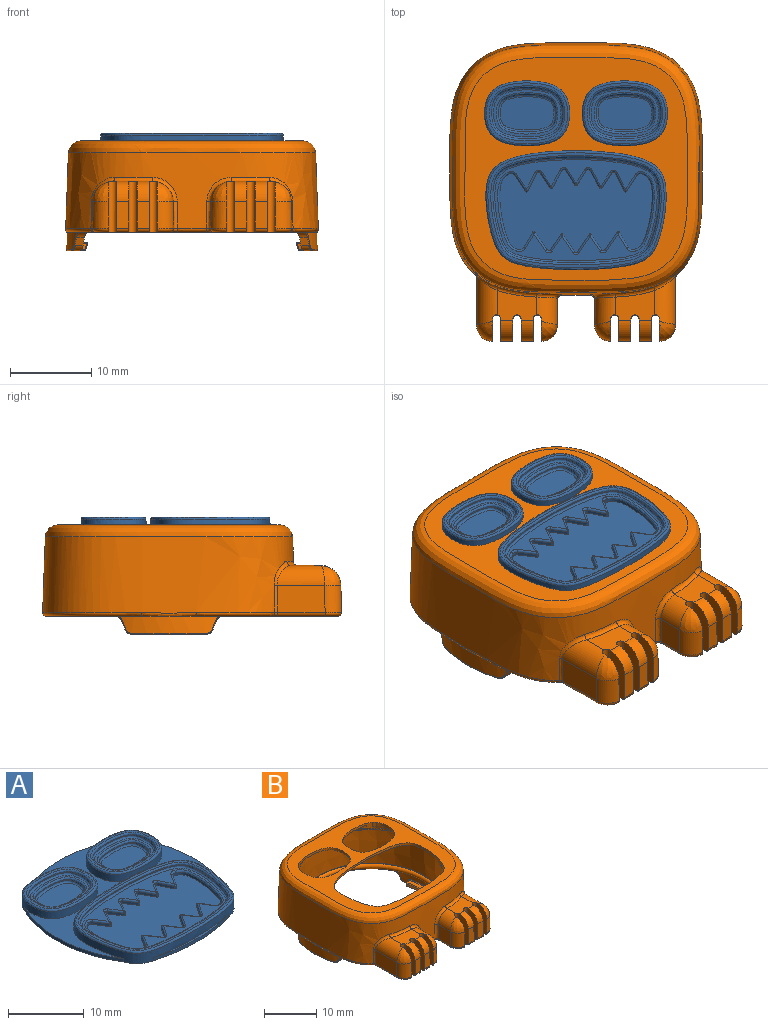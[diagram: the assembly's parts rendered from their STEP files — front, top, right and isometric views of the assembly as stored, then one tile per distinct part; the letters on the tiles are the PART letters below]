
ASSEMBLY  parts=2 mates=1
PART A: 119 faces, bbox 25.6x25.6x2.2 mm
  f0: plane 21.64x14.15mm, normal (0,0,1), area 21.1mm2, adj f114,f116
  f1: plane 9.97x7.48mm, normal (0,0,1), area 9.6mm2, adj f27,f29
  f2: plane 9.97x7.48mm, normal (0,0,1), area 9.6mm2, adj f25,f30
  f3: cylinder r=17.94mm len=17.52mm, axis (0,0,-1), area 9.2mm2, adj f6,f7,f8,f12
  f4: cylinder r=17.8mm len=18mm, axis (0,0,-1), area 9.4mm2, adj f6,f7,f11,f12
  f5: cylinder r=17.94mm len=17.52mm, axis (0,0,-1), area 9.2mm2, adj f6,f7,f8,f11
  f6: plane 25.63x22.38mm, normal (0,0,1), area 121.4mm2, adj f3,f4,f5,f8,f11,f12
  f7: plane 25.63x25.59mm, normal (0,0,-1), area 546.4mm2, adj f3,f4,f5,f8,f9,f11,f12,f117
  f8: extruded ~22.13x14.64mm, area 79.2mm2, adj f3,f5,f6,f7,f9,f10,f116
  f9: cylinder r=24.02mm len=14.06mm, axis (0,0,-1), area 7.1mm2, adj f7,f8,f10
  f10: plane 14.76x1.4mm, normal (0,0,1), area 3.3mm2, adj f8,f9
  f11: extruded ~10.45x7.96mm, area 37.8mm2, adj f4,f5,f6,f7,f29
  f12: extruded ~10.46x7.97mm, area 37.7mm2, adj f3,f4,f6,f7,f30
  f13: extruded ~8.77x6.28mm, area 3.7mm2, adj f25,f26
  f14: plane 8.27x5.78mm, normal (0,0,1), area 7.7mm2, adj f21,f26
  f15: extruded ~8.77x6.28mm, area 3.7mm2, adj f27,f28
  f16: plane 8.27x5.78mm, normal (0,0,1), area 7.7mm2, adj f22,f28
  f17: extruded ~7.06x4.57mm, area 2.9mm2, adj f22,f24
  f18: plane 6.57x4.08mm, normal (0,0,1), area 23.2mm2, adj f24
  f19: extruded ~7.06x4.57mm, area 2.9mm2, adj f21,f23
  f20: plane 6.57x4.08mm, normal (0,0,1), area 23.2mm2, adj f23
  f21: bspline ~7.57x5.08mm, area 7.9mm2, adj f14,f19
  f22: bspline ~7.57x5.08mm, area 7.9mm2, adj f16,f17
  f23: bspline ~7.07x4.59mm, area 7.4mm2, adj f19,f20
  f24: bspline ~7.07x4.59mm, area 7.4mm2, adj f17,f18
  f25: bspline ~9.27x6.78mm, area 10mm2, adj f2,f13
  f26: bspline ~8.77x6.28mm, area 9.5mm2, adj f13,f14
  f27: bspline ~9.27x6.78mm, area 10mm2, adj f1,f15
  f28: bspline ~8.77x6.28mm, area 9.5mm2, adj f15,f16
  f29: bspline ~10.47x7.98mm, area 11.6mm2, adj f1,f11
  f30: bspline ~10.47x7.98mm, area 11.6mm2, adj f2,f12
  f31: extruded ~20.4x12.91mm, area 8.6mm2, adj f114,f115
  f32: plane 19.94x12.45mm, normal (0,0,1), area 60.1mm2, adj f75,f76,f77,f78,f79,f80,f82,f83
  f33: plane 18.75x10.19mm, normal (0,0,1), area 141mm2, adj f34,f35,f36,f37,f38,f39,f40,f41
  f34: plane 1.89x1.14mm, normal (0.86,0.52,0), area 0.9mm2, adj f33,f68,f72,f84
  f35: plane 1.81x1.16mm, normal (0.84,-0.54,0), area 0.9mm2, adj f33,f36,f59,f87
  f36: cylinder r=0.25mm len=0.43mm, axis (0,0,1), area 0.2mm2, adj f33,f35,f37,f85
  f37: plane 2.17x1.2mm, normal (-0.88,-0.48,0), area 1mm2, adj f33,f36,f63,f83
  f38: plane 2.17x1.2mm, normal (0.88,-0.48,0), area 1mm2, adj f33,f39,f58,f95
  f39: cylinder r=0.25mm len=0.43mm, axis (0,0,1), area 0.2mm2, adj f33,f38,f40,f93
  f40: plane 1.81x1.16mm, normal (-0.84,-0.54,0), area 0.9mm2, adj f33,f39,f59,f91
  f41: plane 2.23x1.11mm, normal (0.89,-0.45,0), area 1mm2, adj f33,f42,f57,f103
  f42: cylinder r=0.25mm len=0.43mm, axis (0,0,1), area 0.2mm2, adj f33,f41,f43,f101
  f43: plane 1.89x1.23mm, normal (-0.84,-0.55,0), area 0.9mm2, adj f33,f42,f58,f99
  f44: plane 1.89x1.14mm, normal (-0.86,0.52,0), area 0.9mm2, adj f33,f52,f56,f112
  f45: plane 1.92x1.29mm, normal (-0.83,0.56,0), area 0.9mm2, adj f33,f46,f51,f104
  f46: cylinder r=0.25mm len=0.41mm, axis (0,0,1), area 0.2mm2, adj f33,f45,f47,f106
  f47: plane 2.21x1.5mm, normal (0.83,0.56,0), area 1.1mm2, adj f33,f46,f52,f108
  f48: plane 2.15x1.43mm, normal (-0.83,0.55,0), area 1mm2, adj f33,f49,f73,f96
  f49: cylinder r=0.21mm len=0.4mm, axis (0,0,1), area 0.2mm2, adj f33,f48,f50,f98
  f50: plane 2.15x1.43mm, normal (0.83,0.55,0), area 1mm2, adj f33,f49,f51,f100
  f51: cylinder r=0.15mm len=0.4mm, axis (0,0,1), area 0.1mm2, adj f33,f45,f50,f102
  f52: cylinder r=0.15mm len=0.4mm, axis (0,0,1), area 0.1mm2, adj f33,f44,f47,f110
  f53: extruded ~9.27x2.15mm, area 4.1mm2, adj f33,f54,f56,f111
  f54: cylinder r=0.5mm len=0.64mm, axis (0,0,1), area 0.3mm2, adj f33,f53,f55,f109
  f55: plane 1.98x1.32mm, normal (-0.83,-0.55,0), area 1mm2, adj f33,f54,f57,f107
  f56: cylinder r=0.69mm len=0.78mm, axis (0,0,1), area 0.4mm2, adj f33,f44,f53,f113
  f57: cylinder r=0.15mm len=0.4mm, axis (0,0,1), area 0.1mm2, adj f33,f41,f55,f105
  f58: cylinder r=0.15mm len=0.4mm, axis (0,0,1), area 0.1mm2, adj f33,f38,f43,f97
  f59: cylinder r=0.15mm len=0.4mm, axis (0,0,1), area 0.1mm2, adj f33,f35,f40,f89
  f60: plane 1.89x1.23mm, normal (0.84,-0.55,0), area 0.9mm2, adj f33,f61,f63,f79
  f61: cylinder r=0.25mm len=0.43mm, axis (0,0,1), area 0.2mm2, adj f33,f60,f62,f77
  f62: plane 2.23x1.11mm, normal (-0.89,-0.45,0), area 1mm2, adj f33,f61,f67,f75
  f63: cylinder r=0.15mm len=0.4mm, axis (0,0,1), area 0.1mm2, adj f33,f37,f60,f81
  f64: plane 1.97x1.31mm, normal (0.83,-0.55,0), area 0.9mm2, adj f33,f65,f67,f76
  f65: cylinder r=0.52mm len=0.67mm, axis (0,0,1), area 0.3mm2, adj f33,f64,f66,f78
  f66: extruded ~9.26x2.15mm, area 4.1mm2, adj f33,f65,f68,f80
  f67: cylinder r=0.15mm len=0.4mm, axis (0,0,1), area 0.1mm2, adj f33,f62,f64,f74
  f68: cylinder r=0.69mm len=0.78mm, axis (0,0,1), area 0.4mm2, adj f33,f34,f66,f82
  f69: plane 2.21x1.5mm, normal (-0.83,0.56,0), area 1.1mm2, adj f33,f70,f72,f88
  f70: cylinder r=0.25mm len=0.41mm, axis (0,0,1), area 0.2mm2, adj f33,f69,f71,f90
  f71: plane 1.92x1.29mm, normal (0.83,0.56,0), area 0.9mm2, adj f33,f70,f73,f92
  f72: cylinder r=0.15mm len=0.4mm, axis (0,0,1), area 0.1mm2, adj f33,f34,f69,f86
  f73: cylinder r=0.15mm len=0.4mm, axis (0,0,1), area 0.1mm2, adj f33,f48,f71,f94
  f74: bspline ~0.5x0.27mm, area 0.1mm2, adj f67,f75,f76
  f75: cylinder r=0.25mm len=2.34mm, axis (0.45,-0.89,0), area 0.9mm2, adj f32,f62,f74,f77
  f76: cylinder r=0.25mm len=2.11mm, axis (0.55,0.83,0), area 0.9mm2, adj f32,f64,f74,f78
  f77: torus R=0.5mm, axis (0,0,1), area 0.3mm2, adj f32,f61,f75,f79
  f78: torus R=0.77mm, axis (0,0,1), area 0.3mm2, adj f32,f65,f76,f80
  f79: cylinder r=0.25mm len=2.02mm, axis (0.55,0.84,0), area 0.9mm2, adj f32,f60,f77,f81
  f80: bspline ~10.14x2.62mm, area 4.1mm2, adj f32,f66,f78,f82
  f81: bspline ~0.49x0.27mm, area 0.1mm2, adj f63,f79,f83
  f82: torus R=0.94mm, axis (0,0,1), area 0.4mm2, adj f32,f68,f80,f84
  f83: cylinder r=0.25mm len=2.29mm, axis (0.48,-0.88,0), area 0.9mm2, adj f32,f37,f81,f85
  f84: cylinder r=0.25mm len=2.02mm, axis (-0.52,0.86,0), area 0.8mm2, adj f32,f34,f82,f86
  f85: torus R=0.5mm, axis (0,0,1), area 0.3mm2, adj f32,f36,f83,f87
  f86: bspline ~0.46x0.27mm, area 0.1mm2, adj f72,f84,f88
  f87: cylinder r=0.25mm len=1.94mm, axis (0.54,0.84,0), area 0.8mm2, adj f32,f35,f85,f89
  f88: cylinder r=0.25mm len=2.35mm, axis (-0.56,-0.83,0), area 1mm2, adj f32,f69,f86,f90
  f89: bspline ~0.46x0.27mm, area 0.1mm2, adj f59,f87,f91
  f90: torus R=0.5mm, axis (0,0,1), area 0.3mm2, adj f32,f70,f88,f92
  f91: cylinder r=0.25mm len=1.94mm, axis (0.54,-0.84,0), area 0.8mm2, adj f32,f40,f89,f93
  f92: cylinder r=0.25mm len=2.06mm, axis (-0.56,0.83,0), area 0.9mm2, adj f32,f71,f90,f94
  f93: torus R=0.5mm, axis (0,0,1), area 0.3mm2, adj f32,f39,f91,f95
  f94: bspline ~0.45x0.27mm, area 0.1mm2, adj f73,f92,f96
  f95: cylinder r=0.25mm len=2.29mm, axis (0.48,0.88,0), area 0.9mm2, adj f32,f38,f93,f97
  f96: cylinder r=0.25mm len=2.29mm, axis (-0.55,-0.83,0), area 1mm2, adj f32,f48,f94,f98
  f97: bspline ~0.49x0.27mm, area 0.1mm2, adj f58,f95,f99
  f98: torus R=0.46mm, axis (0,0,1), area 0.2mm2, adj f32,f49,f96,f100
  f99: cylinder r=0.25mm len=2.02mm, axis (0.55,-0.84,0), area 0.9mm2, adj f32,f43,f97,f101
  f100: cylinder r=0.25mm len=2.29mm, axis (-0.55,0.83,0), area 1mm2, adj f32,f50,f98,f102
  f101: torus R=0.5mm, axis (0,0,1), area 0.3mm2, adj f32,f42,f99,f103
  f102: bspline ~0.45x0.27mm, area 0.1mm2, adj f51,f100,f104
  f103: cylinder r=0.25mm len=2.34mm, axis (0.45,0.89,0), area 0.9mm2, adj f32,f41,f101,f105
  f104: cylinder r=0.25mm len=2.06mm, axis (-0.56,-0.83,0), area 0.9mm2, adj f32,f45,f102,f106
  f105: bspline ~0.5x0.27mm, area 0.1mm2, adj f57,f103,f107
  f106: torus R=0.5mm, axis (0,0,1), area 0.3mm2, adj f32,f46,f104,f108
  f107: cylinder r=0.25mm len=2.12mm, axis (0.55,-0.83,0), area 0.9mm2, adj f32,f55,f105,f109
  f108: cylinder r=0.25mm len=2.35mm, axis (-0.56,0.83,0), area 1mm2, adj f32,f47,f106,f110
  f109: torus R=0.75mm, axis (0,0,1), area 0.3mm2, adj f32,f54,f107,f111
  f110: bspline ~0.46x0.27mm, area 0.1mm2, adj f52,f108,f112
  f111: bspline ~10.15x2.61mm, area 4.2mm2, adj f32,f53,f109,f113
  f112: cylinder r=0.25mm len=2.02mm, axis (-0.52,-0.86,0), area 0.8mm2, adj f32,f44,f110,f113
  f113: torus R=0.94mm, axis (0,0,1), area 0.4mm2, adj f32,f56,f111,f112
  f114: bspline ~20.94x13.45mm, area 22.7mm2, adj f0,f31
  f115: bspline ~20.44x12.95mm, area 22.3mm2, adj f31,f32
  f116: bspline ~22.14x14.65mm, area 24.4mm2, adj f0,f8
  f117: cone r=1.05mm half-angle=2deg, axis (0,0,1), area 1.3mm2, adj f7,f118
  f118: plane 2.09x2.09mm, normal (0,0,-1), area 3.4mm2, adj f117
PART B: 282 faces, bbox 35.3x38.8x19.9 mm
  f0: plane 30.07x17.37mm, normal (0,0,-1), area 95.5mm2, adj f13,f14,f15,f16,f17,f20,f21,f27
  f1: plane 4.87x3.68mm, normal (0,0,1), area 14.3mm2, adj f10,f11,f150,f151,f154,f218,f220,f221
  f2: plane 3.29x1.5mm, normal (0,-1,0.02), area 4.9mm2, adj f10,f15,f220,f225
  f3: plane 3.29x1.5mm, normal (0,-1,0.02), area 4.9mm2, adj f11,f16,f222,f226
  f4: plane 4.87x3.68mm, normal (0,0,1), area 14.3mm2, adj f8,f145,f147,f149,f159,f228,f229,f231
  f5: plane 3.29x1.5mm, normal (0,-1,0.02), area 4.9mm2, adj f8,f13,f232,f233
  f6: cylinder r=2mm len=3.3mm, axis (-0.02,-0.02,-1), area 10.2mm2, adj f12,f17,f139,f219
  f7: cylinder r=2mm len=3.3mm, axis (0.02,-0.02,-1), area 10.2mm2, adj f9,f14,f138,f223
  f8: cylinder r=2.5mm len=2.5mm, axis (1,0,0), area 5.8mm2, adj f4,f5,f232,f233
  f9: bspline ~2.64x2.42mm, area 4.8mm2, adj f7,f150,f223
  f10: cylinder r=2.5mm len=2.5mm, axis (-1,0,0), area 5.8mm2, adj f1,f2,f220,f225
  f11: cylinder r=2.5mm len=2.5mm, axis (-1,0,0), area 5.8mm2, adj f1,f3,f222,f226
  f12: bspline ~2.64x2.42mm, area 4.8mm2, adj f6,f151,f219
  f13: cylinder r=0.5mm len=1.5mm, axis (1,0,0), area 1.2mm2, adj f0,f5,f232,f233
  f14: bspline ~2x1.99mm, area 2.3mm2, adj f0,f7,f173,f223
  f15: cylinder r=0.5mm len=1.5mm, axis (-1,0,0), area 1.2mm2, adj f0,f2,f220,f225
  f16: cylinder r=0.5mm len=1.5mm, axis (-1,0,0), area 1.2mm2, adj f0,f3,f222,f226
  f17: bspline ~2x1.99mm, area 2.3mm2, adj f0,f6,f178,f219
  f18: plane 30.07x11.72mm, normal (0,0,-1), area 45mm2, adj f20,f21,f27,f34,f39,f174,f186,f187
  f19: bspline ~31.02x31.02mm, area 862mm2, adj f152,f153,f154,f155,f156,f157,f158,f159
  f20: cone r=15.12mm half-angle=2deg, axis (0,0,-1), area 23.5mm2, adj f0,f18,f175,f180,f181,f182,f183,f184
  f21: cone r=15.12mm half-angle=2deg, axis (0,0,-1), area 23.5mm2, adj f0,f18,f172,f187,f188,f189,f190,f191
  f22: plane 13.19x2.44mm, normal (0,0,-1), area 4.6mm2, adj f102,f108
  f23: plane 13.37x1.8mm, normal (0,0,-1), area 4.6mm2, adj f103,f109
  f24: plane 13.19x2.44mm, normal (0,0,-1), area 4.6mm2, adj f104,f106
  f25: plane 10.51x1.08mm, normal (0,0,-1), area 3.6mm2, adj f101,f107
  f26: plane 27.38x27.38mm, normal (0,0,1), area 266.9mm2, adj f92,f93,f94,f95,f96,f97,f98,f99
  f27: cone r=14.12mm half-angle=2deg, axis (0,0,-1), area 59.9mm2, adj f0,f18,f28,f29,f30,f31,f32,f33
  f28: plane 1.15x0.94mm, normal (0,-0.94,-0.34), area 1mm2, adj f27,f38,f40,f181
  f29: plane 1.15x0.94mm, normal (0,0.94,-0.34), area 1mm2, adj f27,f39,f41,f185
  f30: plane 9.02x2.13mm, normal (0,0,-1), area 13.4mm2, adj f27,f40,f41,f55,f58,f61,f81,f87
  f31: plane 1.15x0.94mm, normal (0,-0.94,-0.34), area 1mm2, adj f27,f35,f37,f192
  f32: plane 1.15x0.94mm, normal (0,0.94,-0.34), area 1mm2, adj f27,f34,f36,f188
  f33: plane 9.02x2.13mm, normal (0,0,-1), area 13.4mm2, adj f27,f36,f37,f62,f63,f64,f74,f80
  f34: cylinder r=1mm len=1.45mm, axis (1,0,0), area 1.2mm2, adj f18,f27,f32,f187
  f35: cylinder r=1mm len=1.45mm, axis (1,0,0), area 1.2mm2, adj f0,f27,f31,f193
  f36: cylinder r=1mm len=1.25mm, axis (1,0,0), area 1.1mm2, adj f27,f32,f33,f189
  f37: cylinder r=1mm len=1.25mm, axis (1,0,0), area 1.1mm2, adj f27,f31,f33,f191
  f38: cylinder r=1mm len=1.45mm, axis (-1,0,0), area 1.2mm2, adj f0,f27,f28,f180
  f39: cylinder r=1mm len=1.45mm, axis (-1,0,0), area 1.2mm2, adj f18,f27,f29,f186
  f40: cylinder r=1mm len=1.25mm, axis (-1,0,0), area 1.1mm2, adj f27,f28,f30,f182
  f41: cylinder r=1mm len=1.25mm, axis (-1,0,0), area 1.1mm2, adj f27,f29,f30,f184
  f42: plane 7.09x1.32mm, normal (0,0,1), area 6.2mm2, adj f50,f51,f52,f84
  f43: cone r=13.14mm half-angle=20.9deg, axis (0,0,-1), area 5.4mm2, adj f51,f56,f57,f61
  f44: plane 0.91x0.75mm, normal (0.26,-0.97,0), area 0.6mm2, adj f50,f55,f56,f86
  f45: plane 0.91x0.75mm, normal (0.26,0.97,0), area 0.6mm2, adj f52,f57,f58,f82
  f46: plane 7.09x1.32mm, normal (0,0,1), area 6.2mm2, adj f68,f69,f73,f77
  f47: cone r=13.14mm half-angle=20.9deg, axis (0,0,-1), area 5.4mm2, adj f64,f67,f70,f73
  f48: plane 0.91x0.75mm, normal (-0.26,0.97,0), area 0.6mm2, adj f62,f67,f68,f75
  f49: plane 0.91x0.75mm, normal (-0.26,-0.97,0), area 0.6mm2, adj f63,f69,f70,f79
  f50: cylinder r=0.15mm len=0.92mm, axis (0.97,0.26,0), area 0.2mm2, adj f42,f44,f53,f85
  f51: torus R=13.36mm, axis (0,0,1), area 1.9mm2, adj f42,f43,f53,f54
  f52: cylinder r=0.15mm len=0.92mm, axis (-0.97,0.26,0), area 0.2mm2, adj f42,f45,f54,f83
  f53: sphere r=0.15mm, area 0mm2, adj f50,f51,f56
  f54: sphere r=0.15mm, area 0mm2, adj f51,f52,f57
  f55: cylinder r=0.15mm len=0.68mm, axis (-0.97,-0.26,0), area 0.2mm2, adj f30,f44,f59,f87
  f56: bspline ~10.31x3.91mm, area 0.2mm2, adj f43,f44,f53,f59
  f57: bspline ~10.31x3.91mm, area 0.2mm2, adj f43,f45,f54,f60
  f58: cylinder r=0.15mm len=0.68mm, axis (0.97,-0.26,0), area 0.2mm2, adj f30,f45,f60,f81
  f59: sphere r=0.15mm, area 0mm2, adj f55,f56,f61
  f60: sphere r=0.15mm, area 0mm2, adj f57,f58,f61
  f61: torus R=13.65mm, axis (0,0,-1), area 1.2mm2, adj f30,f43,f59,f60
  f62: cylinder r=0.15mm len=0.68mm, axis (-0.97,-0.26,0), area 0.2mm2, adj f33,f48,f65,f74
  f63: cylinder r=0.15mm len=0.68mm, axis (0.97,-0.26,0), area 0.2mm2, adj f33,f49,f66,f80
  f64: torus R=13.65mm, axis (0,0,-1), area 1.2mm2, adj f33,f47,f65,f66
  f65: sphere r=0.15mm, area 0mm2, adj f62,f64,f67
  f66: sphere r=0.15mm, area 0mm2, adj f63,f64,f70
  f67: bspline ~10.31x3.91mm, area 0.2mm2, adj f47,f48,f65,f71
  f68: cylinder r=0.15mm len=0.92mm, axis (0.97,0.26,0), area 0.2mm2, adj f46,f48,f71,f76
  f69: cylinder r=0.15mm len=0.92mm, axis (-0.97,0.26,0), area 0.2mm2, adj f46,f49,f72,f78
  f70: bspline ~10.31x3.91mm, area 0.2mm2, adj f47,f49,f66,f72
  f71: sphere r=0.15mm, area 0.1mm2, adj f67,f68,f73
  f72: sphere r=0.15mm, area 0mm2, adj f69,f70,f73
  f73: torus R=13.36mm, axis (0,0,1), area 1.9mm2, adj f46,f47,f71,f72
  f74: bspline ~0.35x0.34mm, area 0mm2, adj f27,f33,f62,f75
  f75: bspline ~3.76x0.27mm, area 0.2mm2, adj f27,f48,f74,f76
  f76: bspline ~0.37x0.32mm, area 0.1mm2, adj f27,f68,f75,f77
  f77: torus R=14.26mm, axis (0,0,1), area 1.7mm2, adj f27,f46,f76,f78
  f78: bspline ~0.37x0.34mm, area 0.1mm2, adj f27,f69,f77,f79
  f79: bspline ~3.76x0.27mm, area 0.2mm2, adj f27,f49,f78,f80
  f80: bspline ~0.35x0.34mm, area 0mm2, adj f27,f33,f63,f79
  f81: bspline ~0.35x0.34mm, area 0mm2, adj f27,f30,f58,f82
  f82: bspline ~3.76x0.27mm, area 0.2mm2, adj f27,f45,f81,f83
  f83: bspline ~0.37x0.34mm, area 0.1mm2, adj f27,f52,f82,f84
  f84: torus R=14.26mm, axis (0,0,1), area 1.7mm2, adj f27,f42,f83,f85
  f85: bspline ~0.37x0.32mm, area 0.1mm2, adj f27,f50,f84,f86
  f86: bspline ~3.76x0.27mm, area 0.2mm2, adj f27,f44,f85,f87
  f87: bspline ~0.35x0.34mm, area 0mm2, adj f27,f30,f55,f86
  f88: plane 28.65x28.65mm, normal (0,0,1), area 10.1mm2, adj f90,f91
  f89: plane 28.73x28.73mm, normal (0,0,-1), area 13.5mm2, adj f27,f90
  f90: torus R=14.21mm, axis (0,0,-1), area 150.5mm2, adj f88,f89
  f91: cone r=14.12mm half-angle=2deg, axis (0,0,-1), area 723mm2, adj f88,f92,f93,f94,f95,f96,f97,f98
  f92: extruded ~10.44x7.96mm, area 16.7mm2, adj f26,f91,f93,f102,f103,f105,f108,f109
  f93: cylinder r=14.02mm len=1mm, axis (0,0,-1), area 0.8mm2, adj f26,f91,f92
  f94: extruded ~10.44x7.96mm, area 16.7mm2, adj f26,f91,f95,f103,f104,f105,f106,f109
  f95: cylinder r=14.02mm len=1mm, axis (0,0,-1), area 0.8mm2, adj f26,f91,f94
  f96: extruded ~22.12x13.12mm, area 24.8mm2, adj f26,f91,f97,f99,f102,f104,f105,f106
  f97: cylinder r=14.02mm len=1mm, axis (0,0,-1), area 0.9mm2, adj f26,f91,f96,f98
  f98: extruded ~17.62x1.72mm, area 11.4mm2, adj f26,f91,f97,f99,f100,f101,f107
  f99: cylinder r=14.02mm len=1mm, axis (0,0,-1), area 0.9mm2, adj f26,f91,f96,f98
  f100: plane 14.76x1.4mm, normal (0,0,-1), area 3.3mm2, adj f98,f101
  f101: cylinder r=24.02mm len=14.06mm, axis (0,0,-1), area 7.3mm2, adj f25,f98,f100,f107
  f102: cylinder r=17.94mm len=17.52mm, axis (0,0,-1), area 9.5mm2, adj f22,f92,f96,f105,f108
  f103: cylinder r=17.8mm len=18mm, axis (0,0,-1), area 9.8mm2, adj f23,f92,f94,f105,f109
  f104: cylinder r=17.94mm len=17.52mm, axis (0,0,-1), area 9.5mm2, adj f24,f94,f96,f105,f106
  f105: plane 25.63x22.38mm, normal (0,0,-1), area 121.4mm2, adj f92,f94,f96,f102,f103,f104
  f106: torus R=13.29mm, axis (0,0,1), area 22.2mm2, adj f24,f91,f94,f96,f104
  f107: torus R=13.29mm, axis (0,0,1), area 17.8mm2, adj f25,f91,f98,f101
  f108: torus R=13.29mm, axis (0,0,1), area 22.2mm2, adj f22,f91,f92,f96,f102
  f109: torus R=13.29mm, axis (0,0,1), area 22.6mm2, adj f23,f91,f92,f94,f103
  f110: plane 6.72x6.72mm, normal (0,0,-1), area 12mm2, adj f111,f112,f113,f114,f115,f116
  f111: plane 9.26x1.2mm, normal (0.05,1,-0.03), area 9mm2, adj f110,f112,f116,f216
  f112: bspline ~9.26x0.79mm, area 7.5mm2, adj f110,f111,f113,f214
  f113: bspline ~9.25x6.18mm, area 79mm2, adj f110,f112,f114,f212
  f114: bspline ~9.26x0.79mm, area 7.5mm2, adj f110,f113,f115,f213
  f115: plane 9.26x1.2mm, normal (1,0.05,-0.03), area 9mm2, adj f110,f114,f116,f215
  f116: bspline ~9.41x5.67mm, area 73.3mm2, adj f110,f111,f115,f215,f216,f217
  f117: plane 6.76x6.73mm, normal (0,0,-1), area 12.1mm2, adj f118,f119,f120,f121,f122,f123
  f118: bspline ~9.26x0.81mm, area 8.3mm2, adj f117,f119,f123,f208,f210,f211
  f119: plane 9.26x1.2mm, normal (-1,-0.05,-0.03), area 9mm2, adj f117,f118,f120,f208
  f120: bspline ~9.41x5.67mm, area 73.4mm2, adj f117,f119,f121,f206,f207,f208
  f121: plane 9.26x1.2mm, normal (-0.05,-1,-0.03), area 9mm2, adj f117,f120,f122,f207
  f122: bspline ~9.26x0.79mm, area 7.5mm2, adj f117,f121,f123,f209
  f123: bspline ~9.25x6.17mm, area 78.7mm2, adj f117,f118,f122,f211
  f124: plane 6.72x6.72mm, normal (0,0,-1), area 12mm2, adj f125,f126,f127,f128,f129,f130
  f125: bspline ~9.41x6.19mm, area 79mm2, adj f124,f126,f130,f204
  f126: bspline ~9.26x0.79mm, area 7.5mm2, adj f124,f125,f127,f202
  f127: plane 9.26x1.2mm, normal (0.05,-1,-0.03), area 9mm2, adj f124,f126,f128,f200
  f128: bspline ~9.41x5.67mm, area 73.4mm2, adj f124,f127,f129,f200,f201,f203
  f129: plane 9.26x1.21mm, normal (1,-0.05,-0.03), area 9.1mm2, adj f124,f128,f130,f203
  f130: bspline ~9.26x0.79mm, area 7.5mm2, adj f124,f125,f129,f205
  f131: plane 6.76x6.73mm, normal (0,0,-1), area 12.1mm2, adj f132,f133,f134,f135,f136,f137
  f132: bspline ~9.41x6.17mm, area 78.7mm2, adj f131,f133,f137,f198
  f133: bspline ~9.26x0.79mm, area 7.5mm2, adj f131,f132,f134,f196
  f134: plane 9.26x1.21mm, normal (-0.05,1,-0.03), area 9.1mm2, adj f131,f133,f135,f194
  f135: bspline ~9.41x5.67mm, area 73.4mm2, adj f131,f134,f136,f194,f195,f197
  f136: plane 9.26x1.2mm, normal (-1,0.05,-0.03), area 9mm2, adj f131,f135,f137,f197
  f137: bspline ~9.26x0.81mm, area 8.3mm2, adj f131,f132,f136,f197,f198,f199
  f138: plane 3.29x3.27mm, normal (1,0,0.02), area 10.5mm2, adj f7,f150,f156,f173
  f139: plane 5.9x3.29mm, normal (-1,0,0.02), area 19.1mm2, adj f6,f151,f152,f178
  f140: plane 5.9x3.29mm, normal (1,0,0.02), area 19.1mm2, adj f143,f149,f161,f166
  f141: plane 3.29x3.27mm, normal (-1,0,0.02), area 10.5mm2, adj f144,f145,f157,f165
  f142: plane 3.29x1.5mm, normal (0,-1,0.02), area 4.9mm2, adj f147,f162,f228,f235
  f143: cylinder r=2mm len=3.3mm, axis (0.02,-0.02,-1), area 10.2mm2, adj f140,f148,f164,f227
  f144: cylinder r=2mm len=3.3mm, axis (-0.02,-0.02,-1), area 10.2mm2, adj f141,f146,f163,f230
  f145: cylinder r=2.5mm len=3.37mm, axis (0,-1,0), area 11.5mm2, adj f4,f141,f146,f158,f230,f231
  f146: bspline ~2.64x2.42mm, area 4.8mm2, adj f144,f145,f230
  f147: cylinder r=2.5mm len=2.5mm, axis (1,0,0), area 5.8mm2, adj f4,f142,f228,f235
  f148: bspline ~2.64x2.42mm, area 4.8mm2, adj f143,f149,f227
  f149: cylinder r=2.5mm len=5.84mm, axis (0,-1,0), area 18.8mm2, adj f4,f140,f148,f160,f227,f229
  f150: cylinder r=2.5mm len=3.37mm, axis (0,-1,0), area 11.5mm2, adj f1,f9,f138,f155,f221,f223
  f151: cylinder r=2.5mm len=5.84mm, axis (0,-1,0), area 18.8mm2, adj f1,f12,f139,f153,f218,f219
  f152: bspline ~6.79x0.58mm, area 1.4mm2, adj f19,f139,f153,f177
  f153: bspline ~3.52x2.99mm, area 2.6mm2, adj f19,f151,f152,f154
  f154: bspline ~9.61x2.13mm, area 3.7mm2, adj f1,f19,f153,f155
  f155: bspline ~3.64x3.62mm, area 3.2mm2, adj f19,f150,f154,f156
  f156: bspline ~6.89x0.74mm, area 2.6mm2, adj f19,f138,f155,f171
  f157: bspline ~6.89x0.74mm, area 2.6mm2, adj f19,f141,f158,f167
  f158: bspline ~3.64x3.62mm, area 3.2mm2, adj f19,f145,f157,f159
  f159: bspline ~9.61x2.13mm, area 3.7mm2, adj f4,f19,f158,f160
  f160: bspline ~3.52x3.47mm, area 2.6mm2, adj f19,f149,f159,f161
  f161: bspline ~6.79x0.58mm, area 1.4mm2, adj f19,f140,f160,f168
  f162: cylinder r=0.5mm len=1.5mm, axis (1,0,0), area 1.2mm2, adj f0,f142,f228,f235
  f163: bspline ~2x1.99mm, area 2.3mm2, adj f0,f144,f165,f230
  f164: bspline ~2x1.99mm, area 2.3mm2, adj f0,f143,f166,f227
  f165: cylinder r=0.5mm len=3.16mm, axis (0,-1,0), area 2.5mm2, adj f0,f141,f163,f167
  f166: cylinder r=0.5mm len=5.8mm, axis (0,-1,0), area 4.6mm2, adj f0,f140,f164,f168
  f167: bspline ~1.22x1.22mm, area 0.9mm2, adj f0,f157,f165,f169
  f168: bspline ~0.93x0.77mm, area 0.5mm2, adj f0,f161,f166,f170
  f169: bspline ~7.78x0.54mm, area 2.8mm2, adj f0,f19,f167,f171
  f170: bspline ~10.77x4mm, area 8.3mm2, adj f0,f19,f168,f172
  f171: bspline ~1.22x1.22mm, area 0.9mm2, adj f0,f156,f169,f173
  f172: bspline ~7.19x0.59mm, area 3.7mm2, adj f19,f21,f170,f174
  f173: cylinder r=0.5mm len=3.16mm, axis (0,-1,0), area 2.5mm2, adj f0,f14,f138,f171
  f174: bspline ~31.01x12.16mm, area 37.2mm2, adj f18,f19,f172,f175
  f175: bspline ~7.19x0.59mm, area 3.7mm2, adj f19,f20,f174,f176
  f176: bspline ~12x4.98mm, area 8.3mm2, adj f0,f19,f175,f177
  f177: bspline ~1.01x0.7mm, area 0.5mm2, adj f0,f152,f176,f178
  f178: cylinder r=0.5mm len=5.8mm, axis (0,-1,0), area 4.6mm2, adj f0,f17,f139,f177
  f179: bspline ~30.38x30.38mm, area 234mm2, adj f19,f26
  f180: bspline ~1.36x1.02mm, area 0.2mm2, adj f0,f20,f38,f181
  f181: bspline ~8.61x3.22mm, area 0.2mm2, adj f20,f28,f180,f182
  f182: bspline ~1.05x0.89mm, area 0.3mm2, adj f20,f40,f181,f183
  f183: torus R=15.3mm, axis (0,0,-1), area 2.2mm2, adj f20,f30,f182,f184
  f184: bspline ~1.19x0.76mm, area 0.3mm2, adj f20,f41,f183,f185
  f185: bspline ~8.61x3.22mm, area 0.2mm2, adj f20,f29,f184,f186
  f186: bspline ~1.36x1.02mm, area 0.2mm2, adj f18,f20,f39,f185
  f187: bspline ~1.36x1.02mm, area 0.2mm2, adj f18,f21,f34,f188
  f188: bspline ~8.61x3.22mm, area 0.2mm2, adj f21,f32,f187,f189
  f189: bspline ~1.05x0.89mm, area 0.3mm2, adj f21,f36,f188,f190
  f190: torus R=15.3mm, axis (0,0,-1), area 2.2mm2, adj f21,f33,f189,f191
  f191: bspline ~1.19x0.76mm, area 0.3mm2, adj f21,f37,f190,f192
  f192: bspline ~8.61x3.22mm, area 0.2mm2, adj f21,f31,f191,f193
  f193: bspline ~1.36x1.02mm, area 0.2mm2, adj f0,f21,f35,f192
  f194: cylinder r=0.15mm len=1mm, axis (1,0.05,0), area 0.2mm2, adj f0,f134,f135,f195,f196
  f195: bspline ~6.06x5.87mm, area 1.8mm2, adj f0,f135,f194,f197
  f196: bspline ~0.92x0.51mm, area 0.2mm2, adj f0,f133,f194,f198
  f197: cylinder r=0.15mm len=1mm, axis (0.05,1,0), area 0.2mm2, adj f0,f135,f136,f137,f195,f199
  f198: bspline ~7.34x6.83mm, area 2mm2, adj f0,f132,f137,f196,f199
  f199: bspline ~0.89x0.64mm, area 0.2mm2, adj f0,f137,f197,f198
  f200: cylinder r=0.15mm len=1mm, axis (-1,-0.05,0), area 0.2mm2, adj f18,f127,f128,f201,f202
  f201: bspline ~6.06x5.87mm, area 1.8mm2, adj f18,f128,f200,f203
  f202: bspline ~0.92x0.51mm, area 0.2mm2, adj f18,f126,f200,f204
  f203: cylinder r=0.15mm len=1mm, axis (-0.05,-1,0), area 0.2mm2, adj f18,f128,f129,f201,f205
  f204: bspline ~8.01x8.01mm, area 2mm2, adj f18,f125,f202,f205
  f205: bspline ~0.86x0.62mm, area 0.2mm2, adj f18,f130,f203,f204
  f206: bspline ~6.06x5.87mm, area 1.8mm2, adj f18,f120,f207,f208
  f207: cylinder r=0.15mm len=1mm, axis (-1,0.05,0), area 0.2mm2, adj f18,f120,f121,f206,f209
  f208: cylinder r=0.15mm len=1mm, axis (-0.05,1,0), area 0.2mm2, adj f18,f118,f119,f120,f206,f210
  f209: bspline ~0.86x0.62mm, area 0.2mm2, adj f18,f122,f207,f211
  f210: bspline ~0.91x0.56mm, area 0.2mm2, adj f18,f118,f208,f211
  f211: bspline ~7.34x6.83mm, area 2mm2, adj f18,f118,f123,f209,f210
  f212: bspline ~7.48x7.06mm, area 2mm2, adj f0,f113,f213,f214
  f213: bspline ~0.92x0.51mm, area 0.2mm2, adj f0,f114,f212,f215
  f214: bspline ~0.86x0.62mm, area 0.2mm2, adj f0,f112,f212,f216
  f215: cylinder r=0.15mm len=1mm, axis (0.05,-1,0), area 0.2mm2, adj f0,f115,f116,f213,f217
  f216: cylinder r=0.15mm len=1mm, axis (1,-0.05,0), area 0.2mm2, adj f0,f111,f116,f214,f217
  f217: bspline ~6.06x5.87mm, area 1.8mm2, adj f0,f116,f215,f216
  f218: cylinder r=0.5mm len=6.25mm, axis (0,0,-1), area 9.8mm2, adj f0,f1,f151,f219,f220
  f219: plane 8.03x4.59mm, normal (1,0,0), area 15.4mm2, adj f0,f6,f12,f17,f151,f218
  f220: plane 6.25x2.74mm, normal (-1,0,0), area 15.5mm2, adj f0,f1,f2,f10,f15,f218
  f221: cylinder r=0.5mm len=6.25mm, axis (0,0,-1), area 9.8mm2, adj f0,f1,f150,f222,f223
  f222: plane 6.25x2.74mm, normal (1,0,0), area 15.5mm2, adj f0,f1,f3,f11,f16,f221
  f223: plane 8.03x4.59mm, normal (-1,0,0), area 15.4mm2, adj f0,f7,f9,f14,f150,f221
  f224: cylinder r=0.5mm len=6.25mm, axis (0,0,-1), area 9.8mm2, adj f0,f1,f225,f226
  f225: plane 6.25x2.74mm, normal (1,0,0), area 15.5mm2, adj f0,f1,f2,f10,f15,f224
  f226: plane 6.25x2.74mm, normal (-1,0,0), area 15.5mm2, adj f0,f1,f3,f11,f16,f224
  f227: plane 8.03x4.59mm, normal (-1,0,0), area 15.4mm2, adj f0,f143,f148,f149,f164,f229
  f228: plane 6.25x2.74mm, normal (1,0,0), area 15.5mm2, adj f0,f4,f142,f147,f162,f229
  f229: cylinder r=0.5mm len=6.25mm, axis (0,0,-1), area 9.8mm2, adj f0,f4,f149,f227,f228
  f230: plane 8.03x4.59mm, normal (1,0,0), area 15.4mm2, adj f0,f144,f145,f146,f163,f231
  f231: cylinder r=0.5mm len=6.25mm, axis (0,0,-1), area 9.8mm2, adj f0,f4,f145,f230,f232
  f232: plane 6.25x2.74mm, normal (-1,0,0), area 15.5mm2, adj f0,f4,f5,f8,f13,f231
  f233: plane 6.25x2.74mm, normal (1,0,0), area 15.5mm2, adj f0,f4,f5,f8,f13,f234
  f234: cylinder r=0.5mm len=6.25mm, axis (0,0,-1), area 9.8mm2, adj f0,f4,f233,f235
  f235: plane 6.25x2.74mm, normal (-1,0,0), area 15.5mm2, adj f0,f4,f142,f147,f162,f234
  f236: cylinder r=0.15mm len=5mm, axis (0,0,-1), area 1.9mm2, adj f237,f246,f247,f274
  f237: plane 5x2.1mm, normal (1,0,0), area 10.5mm2, adj f236,f238,f247,f276
  f238: plane 6.54x5mm, normal (0.05,-1,0), area 32.7mm2, adj f237,f239,f247,f278
  f239: cylinder r=5.76mm len=5mm, axis (0,0,-1), area 7.4mm2, adj f238,f240,f247,f280
  f240: plane 5x2.69mm, normal (-1,0,0), area 13.4mm2, adj f239,f241,f247,f281
  f241: cylinder r=0.15mm len=5mm, axis (0,0,-1), area 1.9mm2, adj f240,f242,f247,f279
  f242: cylinder r=1.5mm len=5mm, axis (0,0,-1), area 13.6mm2, adj f241,f243,f247,f277
  f243: cylinder r=0.15mm len=5mm, axis (0,0,-1), area 1.3mm2, adj f242,f244,f247,f275
  f244: cylinder r=1.5mm len=5mm, axis (0,0,-1), area 12.9mm2, adj f243,f245,f247,f273
  f245: cylinder r=0.15mm len=5mm, axis (0,0,-1), area 1.3mm2, adj f244,f246,f247,f271
  f246: cylinder r=1.5mm len=5mm, axis (0,0,-1), area 13.6mm2, adj f236,f245,f247,f272
  f247: plane 8x2.84mm, normal (0,0,-1), area 15.9mm2, adj f236,f237,f238,f239,f240,f241,f242,f243
  f248: cylinder r=1.5mm len=5mm, axis (0,0,-1), area 13.6mm2, adj f249,f258,f259,f261
  f249: cylinder r=0.15mm len=5mm, axis (0,0,-1), area 1.9mm2, adj f248,f250,f259,f263
  f250: plane 5x2.69mm, normal (1,0,0), area 13.4mm2, adj f249,f251,f259,f265
  f251: cylinder r=5.76mm len=5mm, axis (0,0,-1), area 7.4mm2, adj f250,f252,f259,f267
  f252: plane 6.54x5mm, normal (-0.05,-1,0), area 32.7mm2, adj f251,f253,f259,f269
  f253: plane 5x2.1mm, normal (-1,0,0), area 10.5mm2, adj f252,f254,f259,f270
  f254: cylinder r=0.15mm len=5mm, axis (0,0,-1), area 1.9mm2, adj f253,f255,f259,f268
  f255: cylinder r=1.5mm len=5mm, axis (0,0,-1), area 13.6mm2, adj f254,f256,f259,f266
  f256: cylinder r=0.15mm len=5mm, axis (0,0,-1), area 1.3mm2, adj f255,f257,f259,f264
  f257: cylinder r=1.5mm len=5mm, axis (0,0,-1), area 12.9mm2, adj f256,f258,f259,f262
  f258: cylinder r=0.15mm len=5mm, axis (0,0,-1), area 1.3mm2, adj f248,f257,f259,f260
  f259: plane 8x2.84mm, normal (0,0,-1), area 15.9mm2, adj f248,f249,f250,f251,f252,f253,f254,f255
  f260: torus R=0.4mm, axis (0,0,1), area 0.2mm2, adj f0,f258,f261,f262
  f261: torus R=1.25mm, axis (0,0,1), area 1mm2, adj f0,f248,f260,f263
  f262: torus R=1.25mm, axis (0,0,1), area 1mm2, adj f0,f257,f260,f264
  f263: torus R=0.4mm, axis (0,0,1), area 0.2mm2, adj f0,f249,f261,f265
  f264: torus R=0.4mm, axis (0,0,1), area 0.2mm2, adj f0,f256,f262,f266
  f265: cylinder r=0.25mm len=3.04mm, axis (0,1,0), area 1.1mm2, adj f0,f250,f263,f267
  f266: torus R=1.25mm, axis (0,0,1), area 1mm2, adj f0,f255,f264,f268
  f267: torus R=5.51mm, axis (0,0,1), area 0.6mm2, adj f0,f251,f265,f269
  f268: torus R=0.4mm, axis (0,0,1), area 0.2mm2, adj f0,f254,f266,f270
  f269: cylinder r=0.25mm len=6.79mm, axis (1,-0.05,0), area 2.6mm2, adj f0,f252,f267,f270
  f270: cylinder r=0.25mm len=2.34mm, axis (0,-1,0), area 0.9mm2, adj f0,f253,f268,f269
  f271: torus R=0.4mm, axis (0,0,1), area 0.2mm2, adj f0,f245,f272,f273
  f272: torus R=1.25mm, axis (0,0,1), area 1mm2, adj f0,f246,f271,f274
  f273: torus R=1.25mm, axis (0,0,1), area 1mm2, adj f0,f244,f271,f275
  f274: torus R=0.4mm, axis (0,0,1), area 0.2mm2, adj f0,f236,f272,f276
  f275: torus R=0.4mm, axis (0,0,1), area 0.2mm2, adj f0,f243,f273,f277
  f276: cylinder r=0.25mm len=2.34mm, axis (0,1,0), area 0.9mm2, adj f0,f237,f274,f278
  f277: torus R=1.25mm, axis (0,0,1), area 1mm2, adj f0,f242,f275,f279
  f278: cylinder r=0.25mm len=6.79mm, axis (1,0.05,0), area 2.6mm2, adj f0,f238,f276,f280
  f279: torus R=0.4mm, axis (0,0,1), area 0.2mm2, adj f0,f241,f277,f281
  f280: torus R=5.51mm, axis (0,0,1), area 0.6mm2, adj f0,f239,f278,f281
  f281: cylinder r=0.25mm len=3.04mm, axis (0,-1,0), area 1.1mm2, adj f0,f240,f279,f280
PLACE A t=(0,0,10.81)mm
PLACE B at identity fixed
MATE fastened A.f6 <-> B.f105  axis (0,0,1) through (-1.69,4.07,11.32)mm
